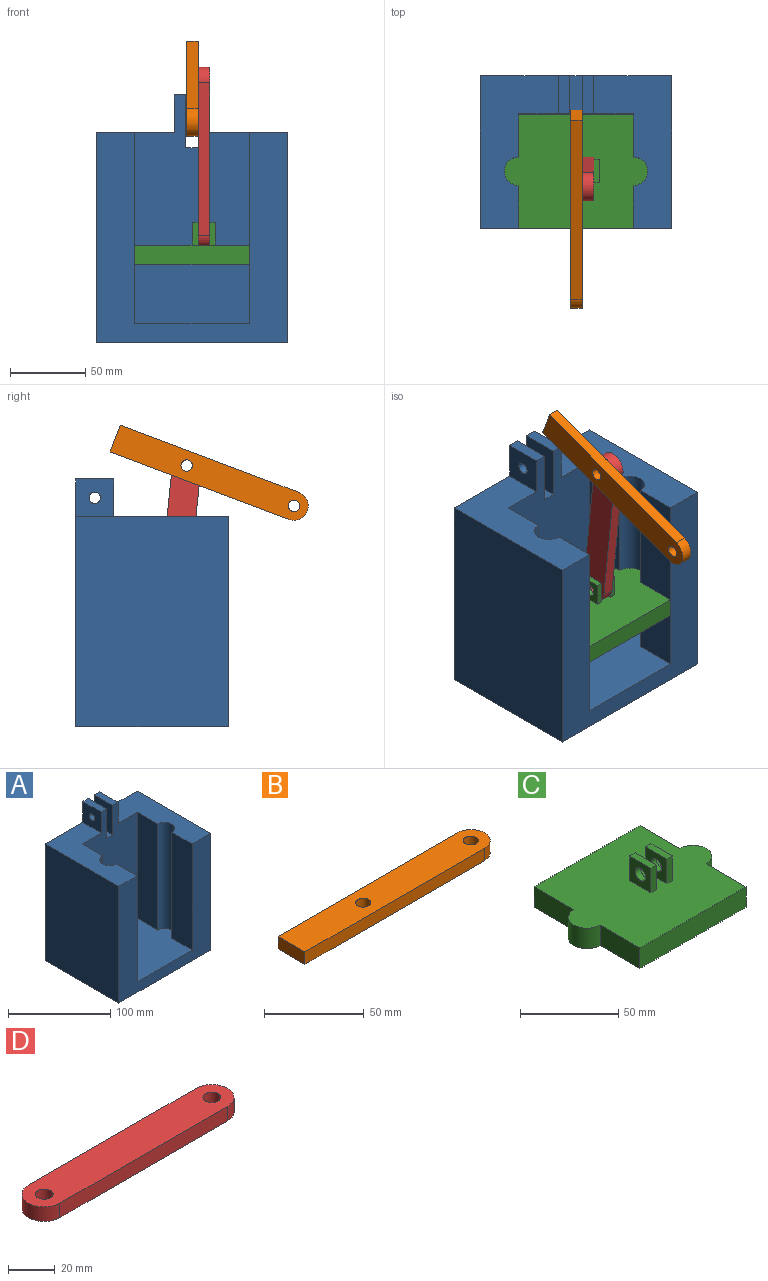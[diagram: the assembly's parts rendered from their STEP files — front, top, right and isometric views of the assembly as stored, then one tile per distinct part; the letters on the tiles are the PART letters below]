
ASSEMBLY  parts=4 mates=3
PART A: 24 faces, bbox 127x101.6x164.7 mm
  f0: plane 101.6x51.82mm, normal (0,0,1), area 3109.1mm2, adj f1,f2,f3,f8,f9,f10,f11,f18
  f1: cylinder r=9.53mm len=127mm, axis (0,0,-1), area 3800.3mm2, adj f0,f2,f11,f13
  f2: plane 127x28.58mm, normal (1,0,0), area 3629mm2, adj f0,f1,f3,f13
  f3: plane 152x76.2mm, normal (0,-1,0), area 9975.8mm2, adj f0,f2,f4,f12,f13,f15,f16,f17
  f4: plane 127x28.58mm, normal (-1,0,0), area 3629mm2, adj f3,f5,f12,f13
  f5: cylinder r=9.53mm len=127mm, axis (0,0,-1), area 3800.3mm2, adj f4,f6,f12,f13
  f6: plane 127x28.58mm, normal (-1,0,0), area 3629mm2, adj f5,f10,f12,f13
  f7: plane 139.7x101.6mm, normal (1,0,0), area 14193.5mm2, adj f8,f10,f12,f14
  f8: plane 164.7x127mm, normal (0,1,0), area 18040.3mm2, adj f0,f7,f9,f12,f14,f15,f16,f17
  f9: plane 139.7x101.6mm, normal (-1,0,0), area 14193.5mm2, adj f0,f8,f10,f14
  f10: plane 139.7x127mm, normal (0,-1,0), area 8064.5mm2, adj f0,f6,f7,f9,f11,f12,f13,f14
  f11: plane 127x28.58mm, normal (1,0,0), area 3629mm2, adj f0,f1,f10,f13
  f12: plane 101.6x51.82mm, normal (0,0,1), area 3109.1mm2, adj f3,f4,f5,f6,f7,f8,f10,f20
  f13: plane 95.25x76.2mm, normal (0,0,1), area 6091.5mm2, adj f1,f2,f3,f4,f5,f6,f10,f11
  f14: plane 127x101.6mm, normal (0,0,-1), area 12903.2mm2, adj f7,f8,f9,f10
  f15: plane 35.16x25.4mm, normal (-1,0,0), area 847.5mm2, adj f3,f8,f17,f21,f22
  f16: plane 35.16x25.4mm, normal (1,0,0), area 847.5mm2, adj f3,f8,f17,f19,f23
  f17: plane 25.4x8.13mm, normal (0,0,1), area 206.5mm2, adj f3,f8,f15,f16
  f18: plane 25.4x25mm, normal (-1,0,0), area 589.4mm2, adj f0,f3,f8,f19,f23
  f19: plane 25.4x7.62mm, normal (0,0,1), area 193.5mm2, adj f3,f8,f16,f18
  f20: plane 25.4x25mm, normal (1,0,0), area 589.4mm2, adj f3,f8,f12,f21,f22
  f21: plane 25.4x7.62mm, normal (0,0,1), area 193.5mm2, adj f3,f8,f15,f20
  f22: cylinder r=3.81mm len=7.62mm, axis (-1,0,0), area 182.4mm2, adj f15,f20
  f23: cylinder r=3.81mm len=7.62mm, axis (-1,0,0), area 182.4mm2, adj f16,f18
PART B: 8 faces, bbox 136.5x19.1x7.6 mm
  f0: plane 127x7.62mm, normal (0,-1,0), area 967.7mm2, adj f1,f4,f6,f7
  f1: cylinder r=9.53mm len=19.05mm, axis (0,0,-1), area 228mm2, adj f0,f2,f6,f7
  f2: plane 127x7.62mm, normal (0,1,0), area 967.7mm2, adj f1,f4,f6,f7
  f3: cylinder r=3.81mm len=7.62mm, axis (0,0,-1), area 182.4mm2, adj f6,f7
  f4: plane 19.05x7.62mm, normal (-1,0,0), area 145.2mm2, adj f0,f2,f6,f7
  f5: cylinder r=3.81mm len=7.62mm, axis (0,0,-1), area 182.4mm2, adj f6,f7
  f6: plane 136.53x19.05mm, normal (0,0,1), area 2470.7mm2, adj f0,f1,f2,f3,f4,f5
  f7: plane 136.53x19.05mm, normal (0,0,-1), area 2470.7mm2, adj f0,f1,f2,f3,f4,f5
PART C: 22 faces, bbox 95.3x76.2x27.9 mm
  f0: plane 95.25x76.2mm, normal (0,0,1), area 5975.3mm2, adj f1,f2,f3,f4,f5,f6,f8,f9
  f1: plane 28.58x12.7mm, normal (1,0,0), area 362.9mm2, adj f0,f4,f7,f9
  f2: plane 28.58x12.7mm, normal (-1,0,0), area 362.9mm2, adj f0,f4,f7,f8
  f3: plane 28.58x12.7mm, normal (1,0,0), area 362.9mm2, adj f0,f6,f7,f9
  f4: plane 76.2x12.7mm, normal (0,1,0), area 967.7mm2, adj f0,f1,f2,f7
  f5: plane 28.58x12.7mm, normal (-1,0,0), area 362.9mm2, adj f0,f6,f7,f8
  f6: plane 76.2x12.7mm, normal (0,-1,0), area 967.7mm2, adj f0,f3,f5,f7
  f7: plane 95.25x76.2mm, normal (0,0,-1), area 6091.5mm2, adj f1,f2,f3,f4,f5,f6,f8,f9
  f8: cylinder r=9.53mm len=19.05mm, axis (0,0,1), area 380mm2, adj f0,f2,f5,f7
  f9: cylinder r=9.53mm len=19.05mm, axis (0,0,1), area 380mm2, adj f0,f1,f3,f7
  f10: plane 15.24x15.24mm, normal (-1,0,0), area 186.7mm2, adj f0,f11,f13,f14,f21
  f11: plane 15.24x3.81mm, normal (0,-1,0), area 58.1mm2, adj f0,f10,f12,f14
  f12: plane 15.24x15.24mm, normal (1,0,0), area 186.7mm2, adj f0,f11,f13,f14,f21
  f13: plane 15.24x3.81mm, normal (0,1,0), area 58.1mm2, adj f0,f10,f12,f14
  f14: plane 15.24x3.81mm, normal (0,0,1), area 58.1mm2, adj f10,f11,f12,f13
  f15: plane 15.24x15.24mm, normal (1,0,0), area 186.7mm2, adj f0,f16,f18,f19,f20
  f16: plane 15.24x3.81mm, normal (0,1,0), area 58.1mm2, adj f0,f15,f17,f19
  f17: plane 15.24x15.24mm, normal (-1,0,0), area 186.7mm2, adj f0,f16,f18,f19,f20
  f18: plane 15.24x3.81mm, normal (0,-1,0), area 58.1mm2, adj f0,f15,f17,f19
  f19: plane 15.24x3.81mm, normal (0,0,1), area 58.1mm2, adj f15,f16,f17,f18
  f20: cylinder r=3.81mm len=7.62mm, axis (1,0,0), area 91.2mm2, adj f15,f17
  f21: cylinder r=3.81mm len=7.62mm, axis (1,0,0), area 91.2mm2, adj f10,f12
PART D: 8 faces, bbox 120.7x19.1x7.6 mm
  f0: plane 101.6x7.62mm, normal (0,-1,0), area 774.2mm2, adj f1,f4,f6,f7
  f1: cylinder r=9.53mm len=19.05mm, axis (0,0,-1), area 228mm2, adj f0,f2,f6,f7
  f2: plane 101.6x7.62mm, normal (0,1,0), area 774.2mm2, adj f1,f4,f6,f7
  f3: cylinder r=3.81mm len=7.62mm, axis (0,0,-1), area 182.4mm2, adj f6,f7
  f4: cylinder r=9.53mm len=19.05mm, axis (0,0,-1), area 228mm2, adj f0,f2,f6,f7
  f5: cylinder r=3.81mm len=7.62mm, axis (0,0,-1), area 182.4mm2, adj f6,f7
  f6: plane 120.65x19.05mm, normal (0,0,1), area 2129.3mm2, adj f0,f1,f2,f3,f4,f5
  f7: plane 120.65x19.05mm, normal (0,0,-1), area 2129.3mm2, adj f0,f1,f2,f3,f4,f5
PLACE A t=(-0.21,-0.25,-57.35)mm fixed
PLACE B rot(axis=(0.64,-0.44,-0.64),132.5deg) t=(3.88,-35.15,99.09)mm
PLACE C t=(-0.21,-12.95,-17.83)mm
PLACE D rot(axis=(-0.71,-0.04,0.71),175.9deg) t=(11.5,-18.11,53.03)mm
MATE revolute D.f3 <-> B.f3  axis (1,0,0) through (3.88,-23.26,103.57)mm
MATE revolute D.f1 <-> C.f20  axis (1,0,0) through (11.5,-12.95,2.49)mm
MATE slider C.f9 <-> A.f5  axis (0,0,1) through (37.89,-12.95,-5.13)mm
